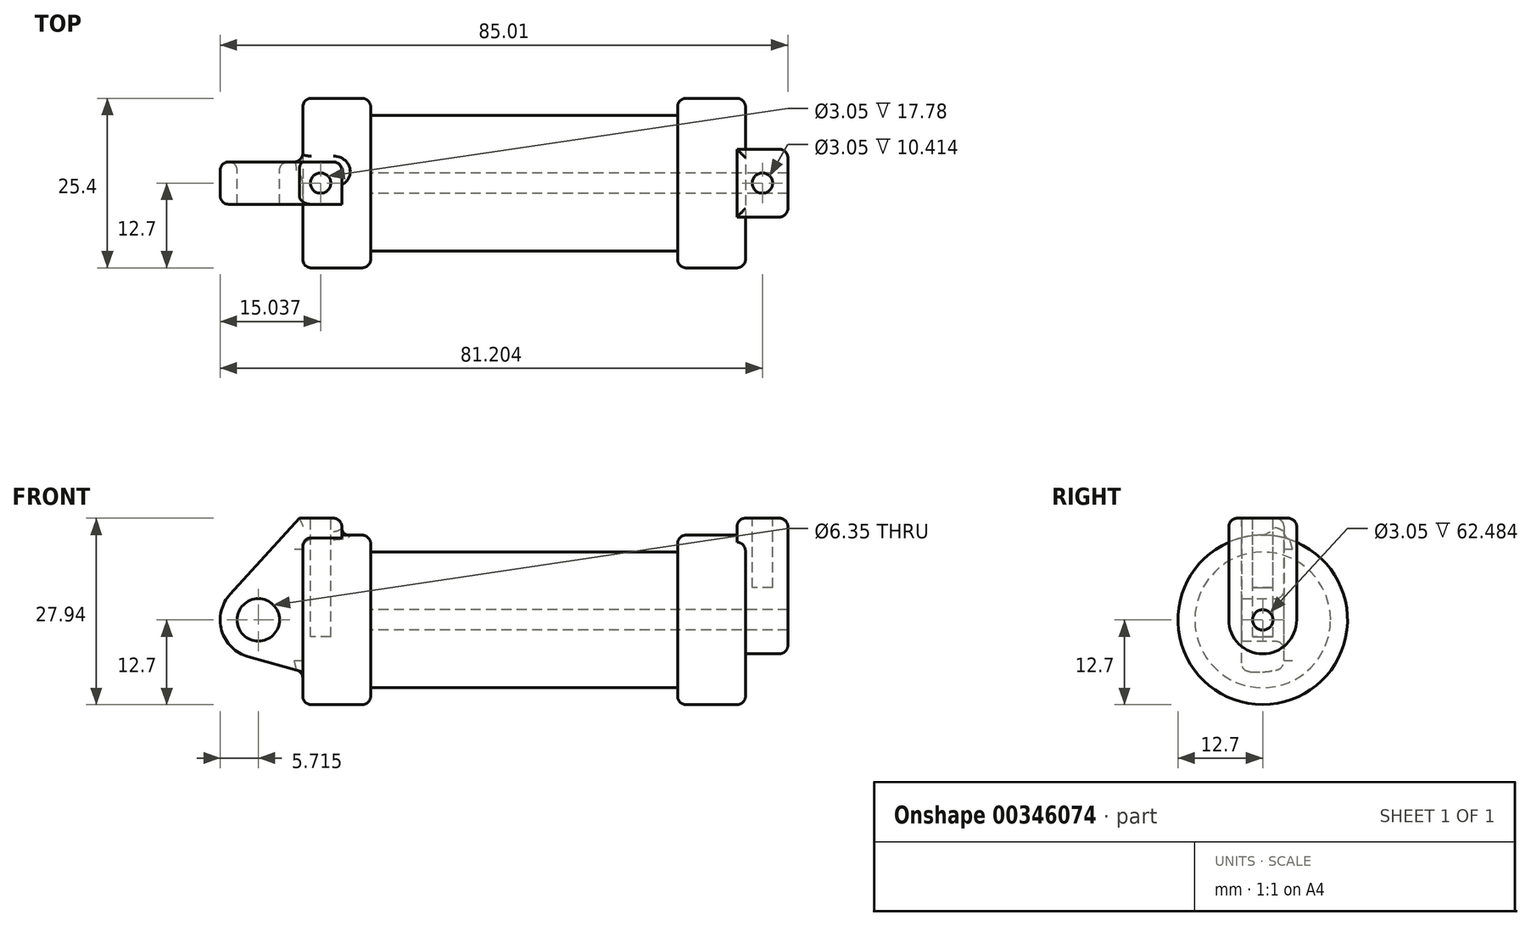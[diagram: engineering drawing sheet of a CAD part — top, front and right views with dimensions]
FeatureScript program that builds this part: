
annotation { "Feature Type Name" : "Feature", "Feature Type Description" : "" }
export const myFeature = defineFeature(function(context is Context, id is Id, definition is map)
    precondition{}
    {
        {
            var Q0;
            Q0=qCreatedBy(makeId("Front.planeOp"),FACE);
            var sketch = newSketch(context, id + "F0", { "sketchPlane" : qUnion([Q0])});
            skLineSegment(sketch, "E0", {"start": v(10.16, 12.7) * mm, "end": v(10.16, 10.16) * mm});
            skLineSegment(sketch, "E1", {"start": v(10.16, 10.16) * mm, "end": v(56.13, 10.16) * mm});
            skLineSegment(sketch, "E2", {"start": v(56.13, 10.16) * mm, "end": v(56.13, 12.7) * mm});
            skLineSegment(sketch, "E3", {"start": v(56.13, 12.7) * mm, "end": v(66.3, 12.7) * mm});
            skLineSegment(sketch, "E4", {"start": v(66.3, 12.7) * mm, "end": v(66.3, 0) * mm});
            skLineSegment(sketch, "E5", {"start": v(66.3, 0) * mm, "end": v(0, 0) * mm});
            skLineSegment(sketch, "E6", {"start": v(5.84, 15.24) * mm, "end": v(-0.5, 15.24) * mm});
            skLineSegment(sketch, "E7", {"start": v(-0.5, 15.24) * mm, "end": v(-10.88, 3.85) * mm});
            skLineSegment(sketch, "E8", {"start": v(0, 0) * mm, "end": v(-6.65, 0) * mm});
            skCircle(sketch, "E9", {"center": v(-6.65, 0) * mm, "radius": 5.72 * mm});
            skCircle(sketch, "E10", {"center": v(-6.65, 0) * mm, "radius": 3.18 * mm});
            skLineSegment(sketch, "E11", {"start": v(5.84, -9.4) * mm, "end": v(-8.18, -5.5) * mm});
            skLineSegment(sketch, "E12", {"start": v(10.16, 12.7) * mm, "end": v(0, 12.7) * mm});
            skLineSegment(sketch, "E13", {"start": v(0, 12.7) * mm, "end": v(0, 0) * mm});
            skLineSegment(sketch, "E14", {"start": v(5.84, 15.24) * mm, "end": v(5.84, -9.4) * mm});
            skLineSegment(sketch, "E15", {"start": v(0, 0) * mm, "end": v(0, -7.78) * mm});
            skSolve(sketch);
        }
        {
            var Q0;
            {var subQ0=sQuery(id+"F0.wireOp",EDGE,"E0");Q0=makeQuery(id+"F0.imprint","IMPRINT",FACE,{"disambiguationData":[TD([[makeQuery(id+"F0.imprint","IMPRINT",EDGE,{"derivedFrom":subQ0}),-1.0]])]});}
            var Q1;
            {var subQ0=sQuery(id+"F0.wireOp",EDGE,"jWTnUyQJ-K3H9-A55l-epBA-AO9HDQuZrJem");Q1=makeQuery(id+"F0.imprint","IMPRINT",FACE,{"disambiguationData":[TD([[makeQuery(id+"F0.imprint","IMPRINT",EDGE,{"derivedFrom":subQ0}),1.0]])]});}
            var Q2;
            {var subQ0=sQuery(id+"F0.wireOp",EDGE,"E13");Q2=makeQuery(id+"F0.imprint","IMPRINT",FACE,{"disambiguationData":[TD([[makeQuery(id+"F0.imprint","IMPRINT",EDGE,{"derivedFrom":subQ0}),1.0]])]});}
            var Q3;
            Q3=sQuery(id+"F0.wireOp",EDGE,"E5");
            revolve(context, id + "F1", {"entities" : qUnion([Q0, Q1, Q2]), "axis" : qUnion([Q3]), "revolveType" : RevolveType.FULL});
        }
        {
            var Q0;
            {var subQ8=sQuery(id+"F0.wireOp",EDGE,"E6");Q0=makeQuery(id+"F0.imprint","IMPRINT",FACE,{"disambiguationData":[TD([[makeQuery(id+"F0.imprint","IMPRINT",EDGE,{"derivedFrom":subQ8}),1.0]])]});}
            var Q1;
            {var subQ0=sQuery(id+"F0.wireOp",EDGE,"E13");Q1=makeQuery(id+"F0.imprint","IMPRINT",FACE,{"disambiguationData":[TD([[makeQuery(id+"F0.imprint","IMPRINT",EDGE,{"derivedFrom":subQ0}),1.0]])]});}
            extrude(context, id + "F2", {"entities" : qUnion([Q0, Q1]), "operationType" : NewBodyOperationType.ADD, "endBound" : BoundingType.SYMMETRIC, "depth" : 6.35 * mm});
        }
        {
            var Q0;
            {var subQ5=sQuery(id+"F0.wireOp",EDGE,"E10");Q0=makeQuery(id+"F0.imprint","IMPRINT",FACE,{"disambiguationData":[TD([[makeQuery(id+"F0.imprint","IMPRINT",EDGE,{"derivedFrom":subQ5}),-1.0]])]});}
            var Q1;
            {var subQ0=sQuery(id+"F0.wireOp",EDGE,"E15");Q1=makeQuery(id+"F0.imprint","IMPRINT",FACE,{"disambiguationData":[TD([[makeQuery(id+"F0.imprint","IMPRINT",EDGE,{"derivedFrom":subQ0}),-1.0]])]});}
            extrude(context, id + "F3", {"entities" : qUnion([Q0, Q1]), "operationType" : NewBodyOperationType.ADD, "endBound" : BoundingType.SYMMETRIC, "depth" : 6.35 * mm});
        }
        {
            var Q0;
            Q0=makeQuery(id+"F1.opRevolve","SWEPT_FACE",FACE,{"disambiguationData":[OSD([sQuery(id+"F0.wireOp",EDGE,"E4")])]});
            var sketch = newSketch(context, id + "F4", { "sketchPlane" : qUnion([Q0])});
            skCircle(sketch, "E16", {"center": v(0, 0) * mm, "radius": 1.52 * mm});
            skCircle(sketch, "E17", {"center": v(0, 0) * mm, "radius": 5.08 * mm});
            skLineSegment(sketch, "E18", {"start": v(-5.08, 15.24) * mm, "end": v(5.08, 15.24) * mm});
            skLineSegment(sketch, "E19", {"start": v(5.08, 15.24) * mm, "end": v(5.08, 0) * mm});
            skLineSegment(sketch, "E20", {"start": v(-5.08, 15.24) * mm, "end": v(-5.08, 0) * mm});
            skSolve(sketch);
        }
        {
            var Q0;
            {var subQ0=sQuery(id+"F4.wireOp",EDGE,"E19");var subQ1=sQuery(id+"F4.wireOp",EDGE,"E17");var subQ2=makeQuery(id+"F4.imprint","INTERSECT",VERTEX,{"derivedFrom":[subQ1,subQ0]});Q0=makeQuery(id+"F4.imprint","IMPRINT",FACE,{"disambiguationData":[TD([[makeQuery(id+"F4.imprint","IMPRINT",EDGE,{"disambiguationData":[TD([[subQ2,-1.0]])],"derivedFrom":subQ1}),-1.0]])]});}
            var Q1;
            Q1=makeQuery(id+"F4.imprint","IMPRINT",FACE,{"disambiguationData":[TD([[makeQuery(id+"F4.imprint","IMPRINT",EDGE,{"derivedFrom":sQuery(id+"F4.wireOp",EDGE,"E16")}),-1.0]])]});
            var Q2;
            {var subQ0=sQuery(id+"F4.wireOp",EDGE,"E18");Q2=makeQuery(id+"F4.imprint","IMPRINT",FACE,{"disambiguationData":[TD([[makeQuery(id+"F4.imprint","IMPRINT",EDGE,{"derivedFrom":subQ0}),-1.0]])]});}
            extrude(context, id + "F5", {"entities" : qUnion([Q0, Q1, Q2]), "operationType" : NewBodyOperationType.ADD, "depth" : 6.35 * mm});
        }
        {
            var Q0;
            {var subQ0=sQuery(id+"F4.wireOp",EDGE,"E18");Q0=makeQuery(id+"F4.imprint","IMPRINT",FACE,{"disambiguationData":[TD([[makeQuery(id+"F4.imprint","IMPRINT",EDGE,{"derivedFrom":subQ0}),-1.0]])]});}
            extrude(context, id + "F6", {"entities" : qUnion([Q0]), "operationType" : NewBodyOperationType.ADD, "oppositeDirection" : true, "depth" : 1.27 * mm});
        }
        {
            var Q0;
            Q0=makeQuery(id+"F5.boolean.opBoolean","SPLIT",FACE,{"disambiguationData":[TD([makeQuery(id+"F5.opExtrude","SWEPT_FACE",FACE,{"disambiguationData":[OSD([sQuery(id+"F4.wireOp",EDGE,"E16")])]})])],"derivedFrom":makeQuery(id+"F1.opRevolve","SWEPT_FACE",FACE,{"disambiguationData":[OSD([sQuery(id+"F0.wireOp",EDGE,"E4")])]})});
            var Q1;
            Q1=sQuery(id+"F4.wireOp",EDGE,"E16");
            var Q2;
            Q2=makeQuery(id+"F1.opRevolve","SWEPT_FACE",FACE,{"disambiguationData":[OSD([sQuery(id+"F0.wireOp",EDGE,"E0")])]});
            extrude(context, id + "F7", {"entities" : qUnion([Q0]), "operationType" : NewBodyOperationType.REMOVE, "surfaceEntities" : qUnion([Q1]), "endBound" : BoundingType.UP_TO_SURFACE, "oppositeDirection" : true, "endBoundEntityFace" : qUnion([Q2]), "depth" : 25.4 * mm});
        }
        {
            var Q0;
            Q0=makeQuery(id+"F2.opExtrude","SWEPT_FACE",FACE,{"disambiguationData":[OSD([sQuery(id+"F0.wireOp",EDGE,"E6")])]});
            var sketch = newSketch(context, id + "F8", { "sketchPlane" : qUnion([Q0])});
            skCircle(sketch, "E21", {"center": v(2.67, 0) * mm, "radius": 1.52 * mm});
            skCircle(sketch, "E22", {"center": v(68.83, 0) * mm, "radius": 1.52 * mm});
            skSolve(sketch);
        }
        {
            var Q0;
            Q0=makeQuery(id+"F1.opRevolve","SWEPT_EDGE",EDGE,{"disambiguationData":[OSD([sQuery(id+"F0.wireOp",EDGE,"E0"),sQuery(id+"F0.wireOp",EDGE,"E12")])]});
            var Q1;
            Q1=makeQuery(id+"F1.opRevolve","SWEPT_EDGE",EDGE,{"disambiguationData":[OSD([sQuery(id+"F0.wireOp",EDGE,"E12"),sQuery(id+"F0.wireOp",EDGE,"E13")])]});
            var Q2;
            Q2=makeQuery(id+"F1.opRevolve","SWEPT_EDGE",EDGE,{"disambiguationData":[OSD([sQuery(id+"F0.wireOp",EDGE,"E2"),sQuery(id+"F0.wireOp",EDGE,"E3")])]});
            var Q3;
            {var subQ0=sQuery(id+"F0.wireOp",EDGE,"E3");var subQ1=sQuery(id+"F0.wireOp",EDGE,"E4");Q3=makeQuery(id+"F5.boolean.opBoolean","SPLIT",EDGE,{"disambiguationData":[topologyDisambiguationEdgeConnected([makeQuery(id+"F1.opRevolve","SWEPT_FACE",FACE,{"disambiguationData":[OSD([subQ1])]})])],"derivedFrom":makeQuery(id+"F1.opRevolve","SWEPT_EDGE",EDGE,{"disambiguationData":[OSD([subQ0,subQ1])]})});}
            var Q4;
            Q4=makeQuery(id+"F5.opExtrude","CAP_EDGE",EDGE,{"disambiguationData":[OSD([sQuery(id+"F4.wireOp",EDGE,"E20")])],"isStart":false});
            var Q5;
            {var subQ0=sQuery(id+"F4.wireOp",EDGE,"E18");Q5=makeQuery(id+"F6.boolean.opBoolean","MERGE",FACE,{"derivedFrom":[makeQuery(id+"F5.opExtrude","SWEPT_FACE",FACE,{"disambiguationData":[OSD([subQ0])]}),makeQuery(id+"F6.opExtrude","SWEPT_FACE",FACE,{"disambiguationData":[OSD([subQ0])]})]});}
            var Q6;
            Q6=makeQuery(id+"F3.opExtrude","CAP_EDGE",EDGE,{"disambiguationData":[OSD([sQuery(id+"F0.wireOp",EDGE,"E11")])],"isStart":false});
            var Q7;
            Q7=makeQuery(id+"F2.opExtrude","SWEPT_EDGE",EDGE,{"disambiguationData":[OSD([sQuery(id+"F0.wireOp",EDGE,"E6"),sQuery(id+"F0.wireOp",EDGE,"E14")])]});
            var Q8;
            {var subQ0=sQuery(id+"F0.wireOp",EDGE,"E9");var subQ1=sQuery(id+"F0.wireOp",EDGE,"E8");Q8=makeQuery(id+"F3.boolean.opBoolean","MERGE",FACE,{"derivedFrom":[makeQuery(id+"F2.opExtrude","CAP_FACE",FACE,{"disambiguationData":[OSD([sQuery(id+"F0.wireOp",EDGE,"E5"),sQuery(id+"F0.wireOp",EDGE,"E6"),sQuery(id+"F0.wireOp",EDGE,"E7"),subQ1,subQ0,sQuery(id+"F0.wireOp",EDGE,"E14")])],"isStart":true}),makeQuery(id+"F3.opExtrude","CAP_FACE",FACE,{"disambiguationData":[OSD([subQ1,subQ0,sQuery(id+"F0.wireOp",EDGE,"E10"),sQuery(id+"F0.wireOp",EDGE,"E11"),sQuery(id+"F0.wireOp",EDGE,"E15")])],"isStart":true})]});}
            fillet(context, id + "F9", {"entities" : qUnion([Q0, Q1, Q2, Q3, Q4, Q5, Q6, Q7, Q8]), "radius" : 1.27 * mm, "tangentPropagation" : true, "allowEdgeOverflow" : false});
        }
        {
            var Q0;
            Q0=makeQuery(id+"F8.imprint","IMPRINT",FACE,{"disambiguationData":[TD([[makeQuery(id+"F8.imprint","IMPRINT",EDGE,{"derivedFrom":sQuery(id+"F8.wireOp",EDGE,"E21")}),1.0]])]});
            var Q1;
            Q1=sQuery(id+"F8.wireOp",EDGE,"E21");
            extrude(context, id + "F10", {"entities" : qUnion([Q0]), "operationType" : NewBodyOperationType.REMOVE, "surfaceEntities" : qUnion([Q1]), "oppositeDirection" : true, "depth" : 17.78 * mm});
        }
        {
            var Q0;
            Q0=makeQuery(id+"F8.imprint","IMPRINT",FACE,{"disambiguationData":[TD([[makeQuery(id+"F8.imprint","IMPRINT",EDGE,{"derivedFrom":sQuery(id+"F8.wireOp",EDGE,"E22")}),1.0]])]});
            var Q1;
            Q1=sQuery(id+"F8.wireOp",EDGE,"E22");
            extrude(context, id + "F11", {"entities" : qUnion([Q0]), "operationType" : NewBodyOperationType.REMOVE, "surfaceEntities" : qUnion([Q1]), "oppositeDirection" : true, "depth" : 10.4 * mm});
        }
    });
